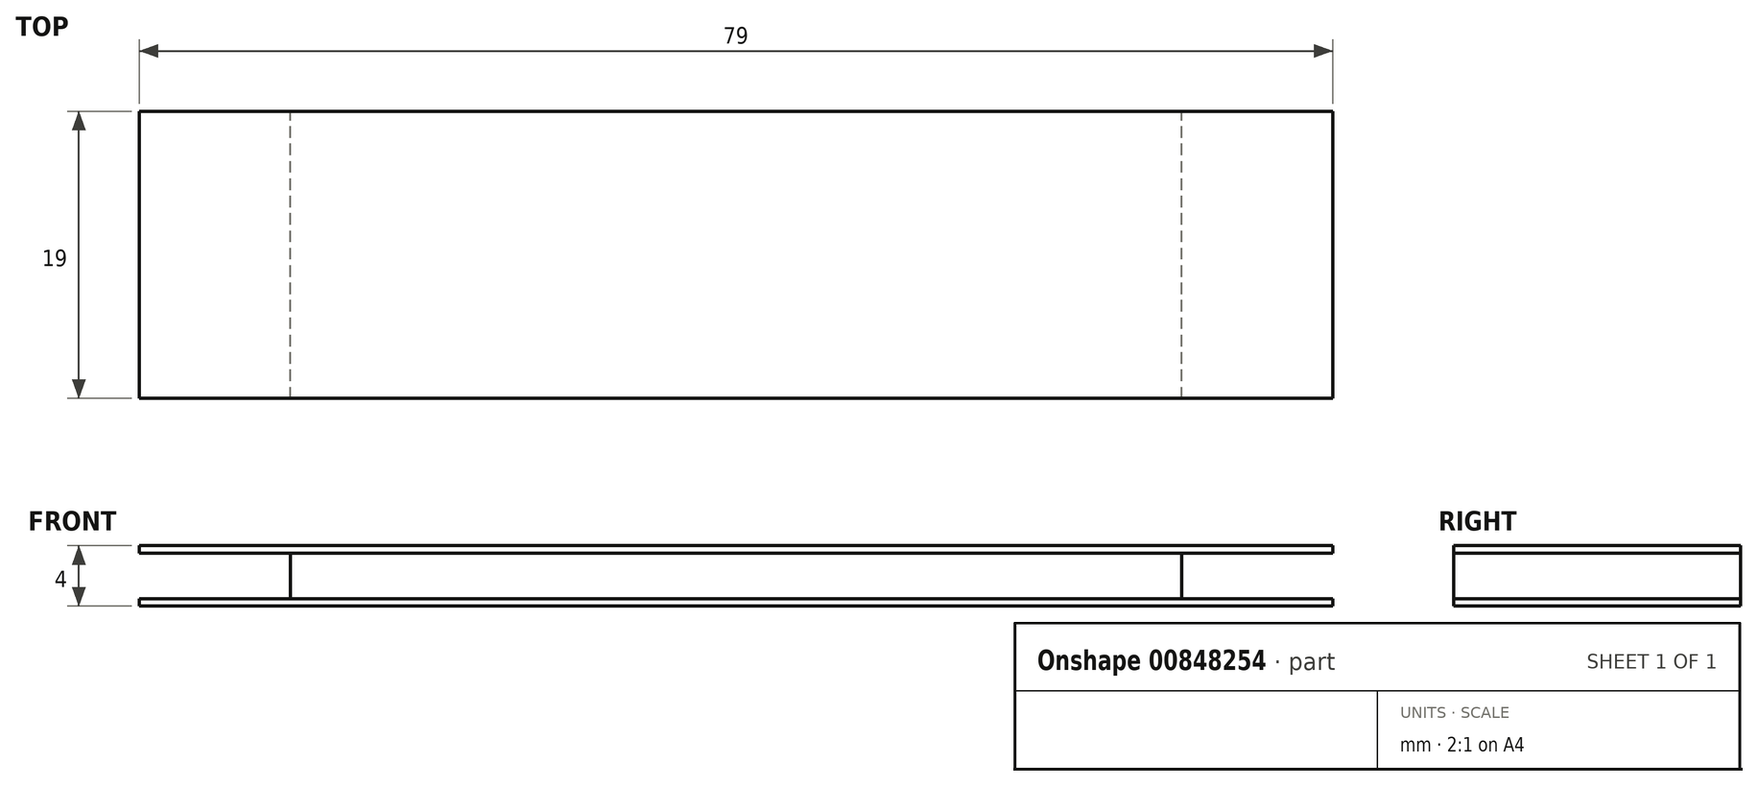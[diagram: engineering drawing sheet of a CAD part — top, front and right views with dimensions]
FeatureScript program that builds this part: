
annotation { "Feature Type Name" : "Feature", "Feature Type Description" : "" }
export const myFeature = defineFeature(function(context is Context, id is Id, definition is map)
    precondition{}
    {
        {
            var Q0;
            Q0=qCreatedBy(makeId("Front.planeOp"),FACE);
            var sketch = newSketch(context, id + "F0", { "sketchPlane" : qUnion([Q0])});
            skLineSegment(sketch, "E0.bottom", {"start": v(29.5, 1.5) * mm, "end": v(-29.5, 1.5) * mm});
            skLineSegment(sketch, "E0.top", {"start": v(29.5, -1.5) * mm, "end": v(-29.5, -1.5) * mm});
            skLineSegment(sketch, "E0.left", {"start": v(29.5, 1.5) * mm, "end": v(29.5, -1.5) * mm});
            skLineSegment(sketch, "E0.right", {"start": v(-29.5, 1.5) * mm, "end": v(-29.5, -1.5) * mm});
            skPoint(sketch, "E0.middle", {"position": v(0, 0) * mm});
            skLineSegment(sketch, "E1.bottom", {"start": v(-39.5, 1.5) * mm, "end": v(39.5, 1.5) * mm});
            skLineSegment(sketch, "E1.top", {"start": v(-39.5, 2) * mm, "end": v(39.5, 2) * mm});
            skLineSegment(sketch, "E1.left", {"start": v(-39.5, 1.5) * mm, "end": v(-39.5, 2) * mm});
            skLineSegment(sketch, "E1.right", {"start": v(39.5, 1.5) * mm, "end": v(39.5, 2) * mm});
            skLineSegment(sketch, "E2.MirrorCS", {"start": v(-39.5, -2) * mm, "end": v(39.5, -2) * mm});
            skLineSegment(sketch, "E3.MirrorCS", {"start": v(-39.5, -1.5) * mm, "end": v(39.5, -1.5) * mm});
            skLineSegment(sketch, "E4.MirrorCS", {"start": v(39.5, -1.5) * mm, "end": v(39.5, -2) * mm});
            skLineSegment(sketch, "E5.MirrorCS", {"start": v(-39.5, -1.5) * mm, "end": v(-39.5, -2) * mm});
            skSolve(sketch);
        }
        {
            var Q0;
            Q0=makeQuery(id+"F0.imprint","IMPRINT",FACE,{"disambiguationData":[TD([[makeQuery(id+"F0.imprint","IMPRINT",EDGE,{"derivedFrom":sQuery(id+"F0.wireOp",EDGE,"E1.top")}),-1.0]])]});
            var Q1;
            Q1=makeQuery(id+"F0.imprint","IMPRINT",FACE,{"disambiguationData":[TD([[makeQuery(id+"F0.imprint","IMPRINT",EDGE,{"derivedFrom":sQuery(id+"F0.wireOp",EDGE,"E2.MirrorCS")}),1.0]])]});
            extrude(context, id + "F1", {"entities" : qUnion([Q0, Q1]), "depth" : 19 * mm, "offsetDistance" : 25 * mm});
        }
        {
            var Q0;
            {var subQ0=sQuery(id+"F0.wireOp",EDGE,"E0.left");Q0=makeQuery(id+"F0.imprint","IMPRINT",FACE,{"disambiguationData":[TD([[makeQuery(id+"F0.imprint","IMPRINT",EDGE,{"derivedFrom":subQ0}),-1.0]])]});}
            extrude(context, id + "F2", {"entities" : qUnion([Q0]), "depth" : 19 * mm, "offsetDistance" : 25 * mm});
        }
    });
